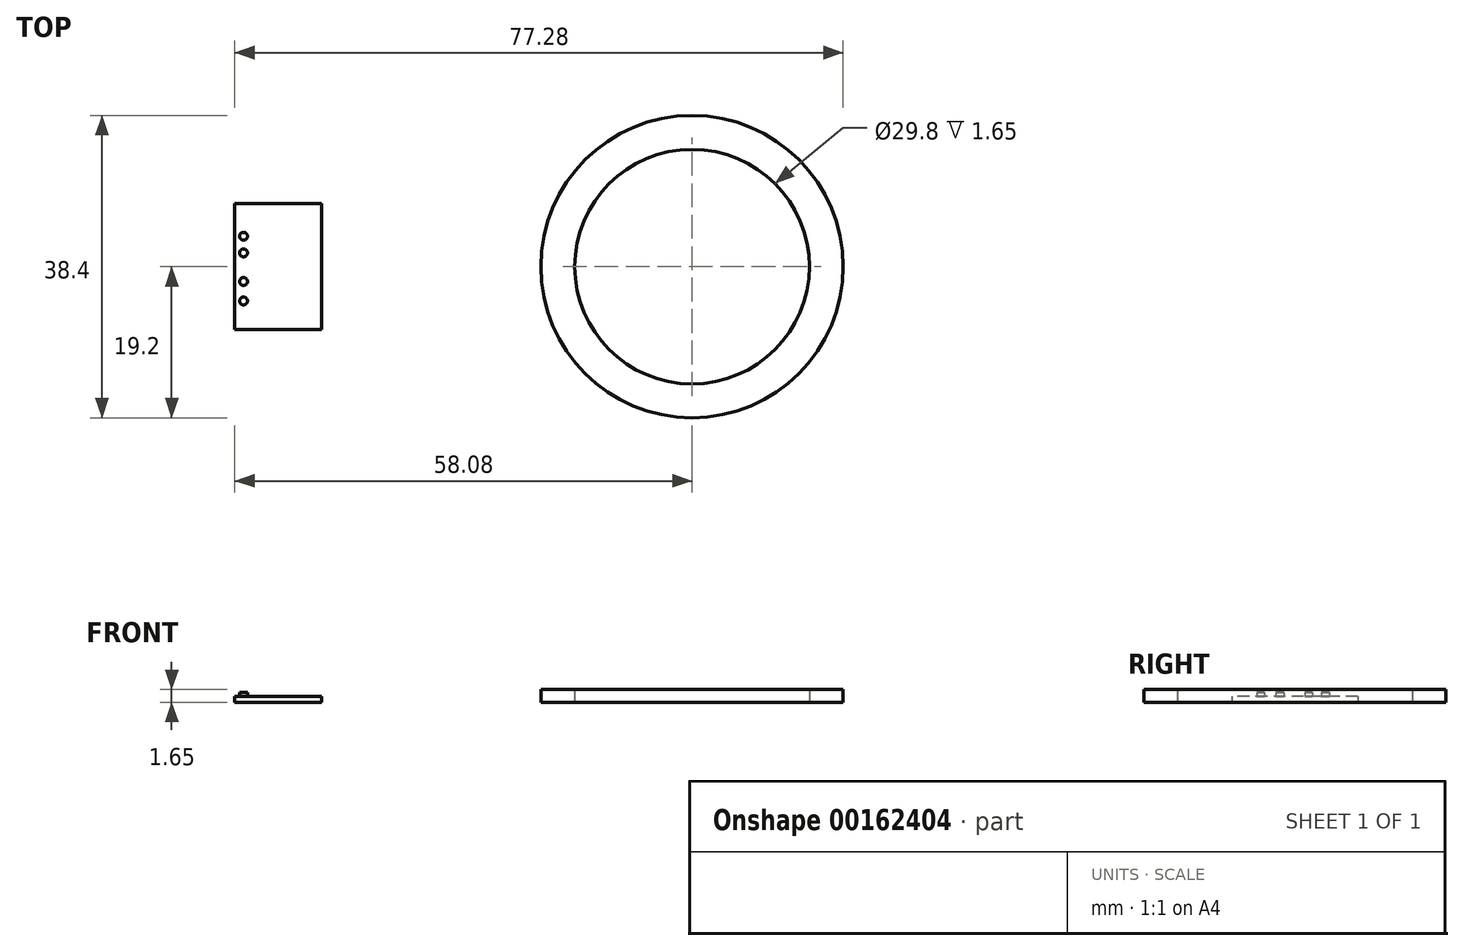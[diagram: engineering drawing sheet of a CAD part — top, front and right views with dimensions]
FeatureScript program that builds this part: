
annotation { "Feature Type Name" : "Feature", "Feature Type Description" : "" }
export const myFeature = defineFeature(function(context is Context, id is Id, definition is map)
    precondition{}
    {
        {
            var Q0;
            Q0=qCreatedBy(makeId("Top.planeOp"),FACE);
            var sketch = newSketch(context, id + "F0", { "sketchPlane" : qUnion([Q0])});
            skCircle(sketch, "E0", {"center": v(0, 0) * mm, "radius": 14.9 * mm});
            skCircle(sketch, "E1", {"center": v(0, 0) * mm, "radius": 19.2 * mm});
            skSolve(sketch);
        }
        {
            var Q0;
            Q0=makeQuery(id+"F0.imprint","IMPRINT",FACE,{"disambiguationData":[TD([[makeQuery(id+"F0.imprint","IMPRINT",EDGE,{"derivedFrom":sQuery(id+"F0.wireOp",EDGE,"E0")}),-1.0]])]});
            extrude(context, id + "F1", {"entities" : qUnion([Q0]), "depth" : 1.65 * mm});
        }
        {
            var Q0;
            Q0=qCreatedBy(makeId("Top.planeOp"),FACE);
            var sketch = newSketch(context, id + "F2", { "sketchPlane" : qUnion([Q0])});
            skLineSegment(sketch, "E2.bottom", {"start": v(-47.08, 8) * mm, "end": v(-58.08, 8) * mm});
            skLineSegment(sketch, "E2.top", {"start": v(-47.08, -8) * mm, "end": v(-58.08, -8) * mm});
            skLineSegment(sketch, "E2.left", {"start": v(-47.08, 8) * mm, "end": v(-47.08, -8) * mm});
            skLineSegment(sketch, "E2.right", {"start": v(-58.08, 8) * mm, "end": v(-58.08, -8) * mm});
            skPoint(sketch, "E2.middle", {"position": v(-52.58, 0) * mm});
            skSolve(sketch);
        }
        {
            var Q0;
            Q0=makeQuery(id+"F2.imprint","IMPRINT",FACE,{"disambiguationData":[TD([[makeQuery(id+"F2.imprint","IMPRINT",EDGE,{"derivedFrom":sQuery(id+"F2.wireOp",EDGE,"E2.bottom")}),1.0]])]});
            extrude(context, id + "F3", {"entities" : qUnion([Q0]), "depth" : 0.75 * mm});
        }
        {
            var Q0;
            Q0=makeQuery(id+"F3.opExtrude","CAP_FACE",FACE,{"disambiguationData":[OSD([sQuery(id+"F2.wireOp",EDGE,"E2.bottom"),sQuery(id+"F2.wireOp",EDGE,"E2.top"),sQuery(id+"F2.wireOp",EDGE,"E2.left"),sQuery(id+"F2.wireOp",EDGE,"E2.right")])],"isStart":false});
            var sketch = newSketch(context, id + "F4", { "sketchPlane" : qUnion([Q0])});
            skLineSegment(sketch, "E3", {"start": v(-56.98, 3.87) * mm, "end": v(-56.98, -4.36) * mm, "construction": true});
            skCircle(sketch, "E4", {"center": v(-56.98, -4.36) * mm, "radius": 0.5 * mm});
            skCircle(sketch, "E5", {"center": v(-56.98, 3.87) * mm, "radius": 0.5 * mm});
            skCircle(sketch, "E6", {"center": v(-56.98, 1.75) * mm, "radius": 0.5 * mm});
            skCircle(sketch, "E7", {"center": v(-56.98, -1.89) * mm, "radius": 0.5 * mm});
            skSolve(sketch);
        }
        {
            var Q0;
            Q0=makeQuery(id+"F4.imprint","IMPRINT",FACE,{"disambiguationData":[TD([[makeQuery(id+"F4.imprint","IMPRINT",EDGE,{"derivedFrom":sQuery(id+"F4.wireOp",EDGE,"E5")}),1.0]])]});
            var Q1;
            Q1=makeQuery(id+"F4.imprint","IMPRINT",FACE,{"disambiguationData":[TD([[makeQuery(id+"F4.imprint","IMPRINT",EDGE,{"derivedFrom":sQuery(id+"F4.wireOp",EDGE,"E6")}),1.0]])]});
            var Q2;
            Q2=makeQuery(id+"F4.imprint","IMPRINT",FACE,{"disambiguationData":[TD([[makeQuery(id+"F4.imprint","IMPRINT",EDGE,{"derivedFrom":sQuery(id+"F4.wireOp",EDGE,"E7")}),1.0]])]});
            var Q3;
            Q3=makeQuery(id+"F4.imprint","IMPRINT",FACE,{"disambiguationData":[TD([[makeQuery(id+"F4.imprint","IMPRINT",EDGE,{"derivedFrom":sQuery(id+"F4.wireOp",EDGE,"E4")}),1.0]])]});
            extrude(context, id + "F5", {"entities" : qUnion([Q0, Q1, Q2, Q3]), "operationType" : NewBodyOperationType.ADD, "depth" : .5 * mm});
        }
    });
